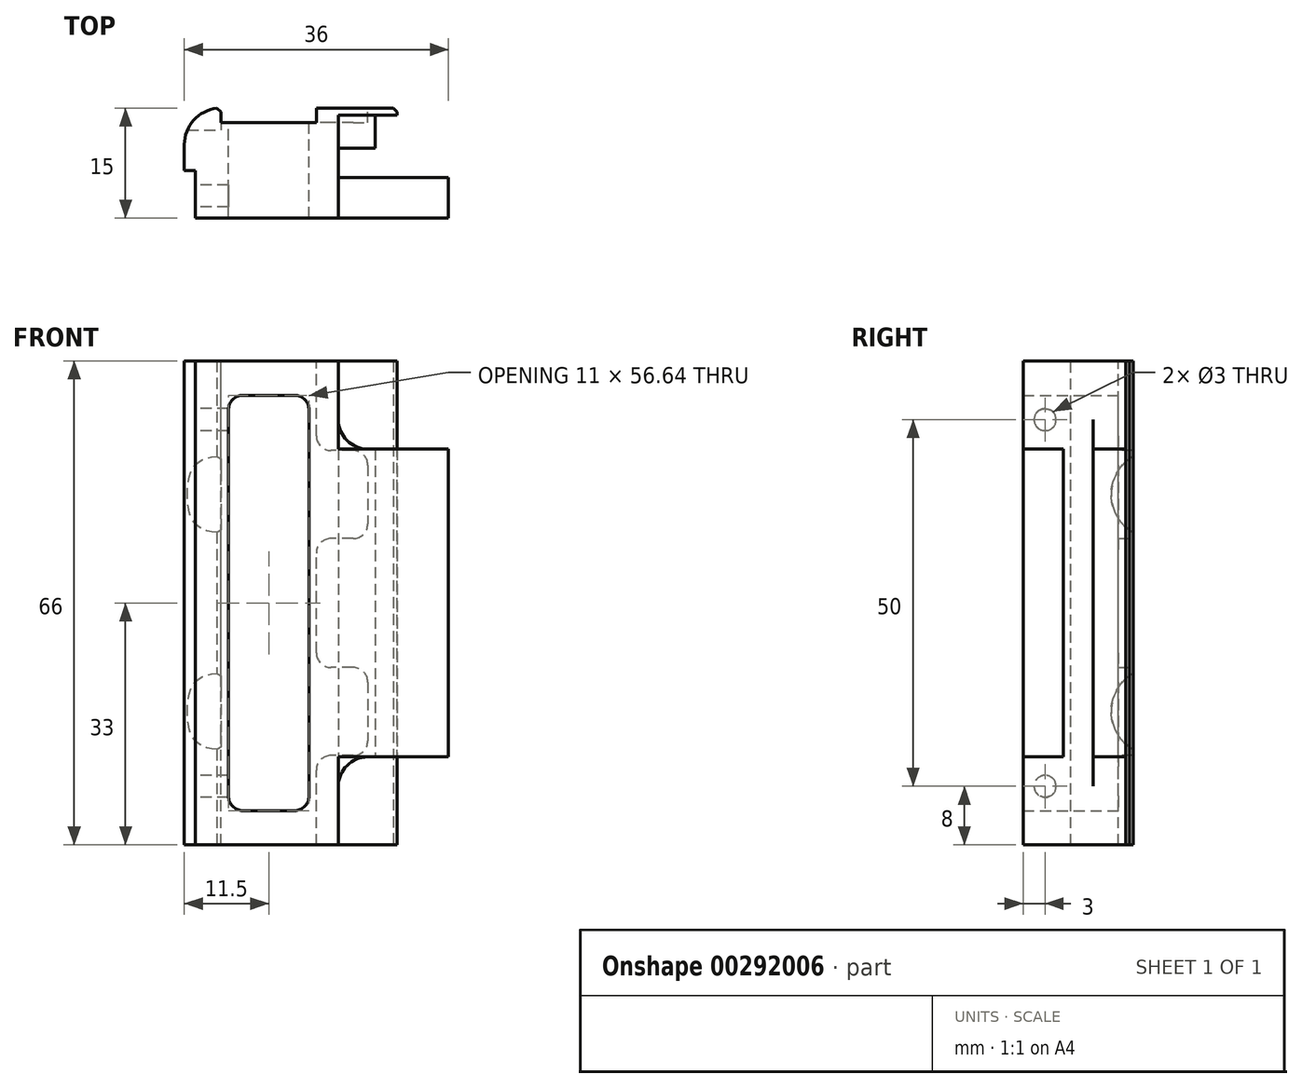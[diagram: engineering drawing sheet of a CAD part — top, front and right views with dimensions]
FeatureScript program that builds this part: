
annotation { "Feature Type Name" : "Feature", "Feature Type Description" : "" }
export const myFeature = defineFeature(function(context is Context, id is Id, definition is map)
    precondition{}
    {
        {
            var Q0;
            Q0=qCreatedBy(makeId("Front.planeOp"),FACE);
            var sketch = newSketch(context, id + "F0", { "sketchPlane" : qUnion([Q0])});
            skLineSegment(sketch, "E0.bottom", {"start": v(5.5, -28.32) * mm, "end": v(-5.5, -28.32) * mm});
            skLineSegment(sketch, "E0.top", {"start": v(5.5, 28.32) * mm, "end": v(-5.5, 28.32) * mm});
            skLineSegment(sketch, "E0.left", {"start": v(5.5, -28.32) * mm, "end": v(5.5, 28.32) * mm});
            skLineSegment(sketch, "E0.right", {"start": v(-5.5, -28.32) * mm, "end": v(-5.5, 28.32) * mm});
            skPoint(sketch, "E0.middle", {"position": v(0, 0) * mm});
            skLineSegment(sketch, "E1.bottom", {"start": v(9.5, -33) * mm, "end": v(-11.5, -33) * mm});
            skLineSegment(sketch, "E1.top", {"start": v(9.5, 33) * mm, "end": v(-11.5, 33) * mm});
            skLineSegment(sketch, "E1.right", {"start": v(-11.5, -33) * mm, "end": v(-11.5, 33) * mm});
            skLineSegment(sketch, "E2", {"start": v(9.5, 33) * mm, "end": v(9.5, -33) * mm});
            skSolve(sketch);
        }
        {
            var Q0;
            Q0=qSketchRegion(id+"F0",true);
            extrude(context, id + "F1", {"entities" : qUnion([Q0]), "depth" : 15 * mm});
        }
        {
            var Q0;
            Q0=makeQuery(id+"F1.opExtrude","CAP_EDGE",EDGE,{"disambiguationData":[OSD([sQuery(id+"F0.wireOp",EDGE,"E1.right")])],"isStart":true});
            fillet(context, id + "F2", {"entities" : qUnion([Q0]), "radius" : 5 * mm, "tangentPropagation" : true, "allowEdgeOverflow" : false});
        }
        {
            var Q0;
            Q0=qCreatedBy(makeId("Front.planeOp"),FACE);
            var sketch = newSketch(context, id + "F3", { "sketchPlane" : qUnion([Q0])});
            skLineSegment(sketch, "E3.bottom", {"start": v(9.5, -21) * mm, "end": v(24.5, -21) * mm});
            skLineSegment(sketch, "E3.top", {"start": v(9.5, 21) * mm, "end": v(24.5, 21) * mm});
            skLineSegment(sketch, "E3.left", {"start": v(9.5, -21) * mm, "end": v(9.5, 21) * mm});
            skLineSegment(sketch, "E3.right", {"start": v(24.5, -21) * mm, "end": v(24.5, 21) * mm});
            skPoint(sketch, "E3.middle", {"position": v(17, 0) * mm});
            skSolve(sketch);
        }
        {
            var Q0;
            Q0=makeQuery(id+"F3.imprint","IMPRINT",FACE,{"disambiguationData":[TD([[makeQuery(id+"F3.imprint","IMPRINT",EDGE,{"derivedFrom":sQuery(id+"F3.wireOp",EDGE,"E3.bottom")}),1.0]])]});
            extrude(context, id + "F4", {"entities" : qUnion([Q0]), "operationType" : NewBodyOperationType.ADD, "depth" : 15 * mm, "hasSecondDirection" : true, "secondDirectionOppositeDirection" : false, "secondDirectionDepth" : 9.5 * mm});
        }
        {
            var Q0;
            Q0=makeQuery(id+"F1.opExtrude","SWEPT_EDGE",EDGE,{"disambiguationData":[OSD([sQuery(id+"F0.wireOp",EDGE,"E0.bottom"),sQuery(id+"F0.wireOp",EDGE,"E0.left")])]});
            var Q1;
            Q1=makeQuery(id+"F1.opExtrude","SWEPT_EDGE",EDGE,{"disambiguationData":[OSD([sQuery(id+"F0.wireOp",EDGE,"E0.bottom"),sQuery(id+"F0.wireOp",EDGE,"E0.right")])]});
            var Q2;
            Q2=makeQuery(id+"F1.opExtrude","SWEPT_EDGE",EDGE,{"disambiguationData":[OSD([sQuery(id+"F0.wireOp",EDGE,"E0.top"),sQuery(id+"F0.wireOp",EDGE,"E0.right")])]});
            var Q3;
            Q3=makeQuery(id+"F1.opExtrude","SWEPT_EDGE",EDGE,{"disambiguationData":[OSD([sQuery(id+"F0.wireOp",EDGE,"E0.top"),sQuery(id+"F0.wireOp",EDGE,"E0.left")])]});
            fillet(context, id + "F5", {"entities" : qUnion([Q0, Q1, Q2, Q3]), "radius" : 2 * mm, "tangentPropagation" : true, "allowEdgeOverflow" : false});
        }
        {
            var Q0;
            Q0=qCreatedBy(makeId("Top.planeOp"),FACE);
            var sketch = newSketch(context, id + "F6", { "sketchPlane" : qUnion([Q0])});
            skLineSegment(sketch, "E4.bottom", {"start": v(-10, -15) * mm, "end": v(-11.5, -15) * mm});
            skLineSegment(sketch, "E4.top", {"start": v(-10, -8.5) * mm, "end": v(-11.5, -8.5) * mm});
            skLineSegment(sketch, "E4.left", {"start": v(-10, -15) * mm, "end": v(-10, -8.5) * mm});
            skLineSegment(sketch, "E4.right", {"start": v(-11.5, -15) * mm, "end": v(-11.5, -8.5) * mm});
            skSolve(sketch);
        }
        {
            var Q0;
            Q0=qSketchRegion(id+"F6",true);
            extrude(context, id + "F7", {"entities" : qUnion([Q0]), "operationType" : NewBodyOperationType.REMOVE, "oppositeDirection" : true, "depth" : 50 * mm, "hasSecondDirection" : true, "secondDirectionOppositeDirection" : false, "secondDirectionDepth" : 50 * mm});
        }
        {
            var Q0;
            Q0=makeQuery(id+"F7.boolean.opBoolean","COPY",FACE,{"derivedFrom":makeQuery(id+"F7.opExtrude","SWEPT_FACE",FACE,{"disambiguationData":[OSD([sQuery(id+"F6.wireOp",EDGE,"E4.left")])]})});
            var sketch = newSketch(context, id + "F8", { "sketchPlane" : qUnion([Q0])});
            skCircle(sketch, "E5", {"center": v(12, 25) * mm, "radius": 1.5 * mm});
            skCircle(sketch, "E6", {"center": v(12, -25) * mm, "radius": 1.5 * mm});
            skSolve(sketch);
        }
        {
            var Q0;
            Q0=qSketchRegion(id+"F8",true);
            extrude(context, id + "F9", {"entities" : qUnion([Q0]), "operationType" : NewBodyOperationType.REMOVE, "oppositeDirection" : true, "depth" : 5 * mm});
        }
        {
            var Q0;
            Q0=qCreatedBy(makeId("Top.planeOp"),FACE);
            var sketch = newSketch(context, id + "F10", { "sketchPlane" : qUnion([Q0])});
            skLineSegment(sketch, "E7.bottom", {"start": v(17.5, -1) * mm, "end": v(14.5, -1) * mm});
            skLineSegment(sketch, "E7.top", {"start": v(17.5, 0) * mm, "end": v(14.5, 0) * mm});
            skLineSegment(sketch, "E7.left", {"start": v(17.5, -1) * mm, "end": v(17.5, 0) * mm});
            skLineSegment(sketch, "E7.right", {"start": v(14.5, -1) * mm, "end": v(14.5, 0) * mm});
            skLineSegment(sketch, "E8.bottom", {"start": v(9.5, 0) * mm, "end": v(14.5, 0) * mm});
            skLineSegment(sketch, "E8.top", {"start": v(9.5, -5.45) * mm, "end": v(14.5, -5.45) * mm});
            skLineSegment(sketch, "E8.left", {"start": v(9.5, 0) * mm, "end": v(9.5, -5.45) * mm});
            skLineSegment(sketch, "E8.right", {"start": v(14.5, 0) * mm, "end": v(14.5, -5.45) * mm});
            skSolve(sketch);
        }
        {
            var Q0;
            Q0=makeQuery(id+"F10.imprint","IMPRINT",FACE,{"disambiguationData":[TD([[makeQuery(id+"F10.imprint","IMPRINT",EDGE,{"derivedFrom":sQuery(id+"F10.wireOp",EDGE,"E7.bottom")}),-1.0]])]});
            var Q1;
            {var subQ2=sQuery(id+"F10.wireOp",EDGE,"E8.bottom");Q1=makeQuery(id+"F10.imprint","IMPRINT",FACE,{"disambiguationData":[TD([[makeQuery(id+"F10.imprint","IMPRINT",EDGE,{"derivedFrom":subQ2}),-1.0]])]});}
            extrude(context, id + "F11", {"entities" : qUnion([Q0, Q1]), "operationType" : NewBodyOperationType.ADD, "depth" : 33 * mm, "hasSecondDirection" : true, "secondDirectionOppositeDirection" : true, "secondDirectionDepth" : 33 * mm});
        }
        {
            var Q0;
            Q0=makeQuery(id+"F11.opExtrude","SWEPT_EDGE",EDGE,{"disambiguationData":[OSD([sQuery(id+"F10.wireOp",EDGE,"E7.top"),sQuery(id+"F10.wireOp",EDGE,"E7.left")])]});
            chamfer(context, id + "F12", {"entities" : qUnion([Q0]), "width" : 0.5 * mm, "tangentPropagation" : true});
        }
        {
            var Q0;
            Q0=makeQuery(id+"F4.boolean.opBoolean","MERGE",FACE,{"derivedFrom":[makeQuery(id+"F1.opExtrude","CAP_FACE",FACE,{"disambiguationData":[OSD([sQuery(id+"F0.wireOp",EDGE,"E0.bottom"),sQuery(id+"F0.wireOp",EDGE,"E0.top"),sQuery(id+"F0.wireOp",EDGE,"E0.left"),sQuery(id+"F0.wireOp",EDGE,"E0.right"),sQuery(id+"F0.wireOp",EDGE,"E1.bottom"),sQuery(id+"F0.wireOp",EDGE,"E1.top"),sQuery(id+"F0.wireOp",EDGE,"E1.right"),sQuery(id+"F0.wireOp",EDGE,"E2")])],"isStart":false}),makeQuery(id+"F4.opExtrude","CAP_FACE",FACE,{"disambiguationData":[OSD([sQuery(id+"F3.wireOp",EDGE,"E3.bottom"),sQuery(id+"F3.wireOp",EDGE,"E3.top"),sQuery(id+"F3.wireOp",EDGE,"E3.left"),sQuery(id+"F3.wireOp",EDGE,"E3.right")])],"isStart":false})]});
            var sketch = newSketch(context, id + "F13", { "sketchPlane" : qUnion([Q0])});
            skLineSegment(sketch, "E9.bottom", {"start": v(9.5, -33) * mm, "end": v(14.5, -33) * mm});
            skLineSegment(sketch, "E9.top", {"start": v(9.5, -21) * mm, "end": v(14.5, -21) * mm});
            skLineSegment(sketch, "E9.left", {"start": v(9.5, -33) * mm, "end": v(9.5, -21) * mm});
            skLineSegment(sketch, "E9.right", {"start": v(14.5, -33) * mm, "end": v(14.5, -21) * mm});
            skLineSegment(sketch, "E10.bottom", {"start": v(9.5, 33) * mm, "end": v(14.5, 33) * mm});
            skLineSegment(sketch, "E10.top", {"start": v(9.5, 21) * mm, "end": v(14.5, 21) * mm});
            skLineSegment(sketch, "E10.left", {"start": v(9.5, 33) * mm, "end": v(9.5, 21) * mm});
            skLineSegment(sketch, "E10.right", {"start": v(14.5, 33) * mm, "end": v(14.5, 21) * mm});
            skSolve(sketch);
        }
        {
            var Q0;
            Q0=qSketchRegion(id+"F13",true);
            extrude(context, id + "F14", {"entities" : qUnion([Q0]), "operationType" : NewBodyOperationType.REMOVE, "oppositeDirection" : true, "depth" : 14 * mm});
        }
        {
            var Q0;
            Q0=makeQuery(id+"F14.boolean.opBoolean","COPY",EDGE,{"derivedFrom":makeQuery(id+"F14.opExtrude","SWEPT_EDGE",EDGE,{"disambiguationData":[OSD([sQuery(id+"F13.wireOp",EDGE,"E9.top"),sQuery(id+"F13.wireOp",EDGE,"E9.left")])]})});
            var Q1;
            Q1=makeQuery(id+"F14.boolean.opBoolean","COPY",EDGE,{"derivedFrom":makeQuery(id+"F14.opExtrude","SWEPT_EDGE",EDGE,{"disambiguationData":[OSD([sQuery(id+"F13.wireOp",EDGE,"E10.top"),sQuery(id+"F13.wireOp",EDGE,"E10.left")])]})});
            var Q2;
            Q2=makeQuery(id+"F4.opExtrude","SWEPT_EDGE",EDGE,{"disambiguationData":[OSD([sQuery(id+"F3.wireOp",EDGE,"E3.top"),sQuery(id+"F3.wireOp",EDGE,"E3.left")])]});
            var Q3;
            Q3=makeQuery(id+"F4.opExtrude","SWEPT_EDGE",EDGE,{"disambiguationData":[OSD([sQuery(id+"F3.wireOp",EDGE,"E3.bottom"),sQuery(id+"F3.wireOp",EDGE,"E3.left")])]});
            fillet(context, id + "F15", {"entities" : qUnion([Q0, Q1, Q2, Q3]), "radius" : 4 * mm, "tangentPropagation" : true, "allowEdgeOverflow" : false});
        }
        {
            var Q0;
            Q0=qCreatedBy(makeId("Front.planeOp"),FACE);
            var sketch = newSketch(context, id + "F16", { "sketchPlane" : qUnion([Q0])});
            skLineSegment(sketch, "E11.bottom", {"start": v(-6.5, -35) * mm, "end": v(6.5, -35) * mm});
            skLineSegment(sketch, "E11.top", {"start": v(-6.5, 35) * mm, "end": v(6.5, 35) * mm});
            skLineSegment(sketch, "E11.left", {"start": v(-6.5, -35) * mm, "end": v(-6.5, 35) * mm});
            skLineSegment(sketch, "E11.right", {"start": v(6.5, -35) * mm, "end": v(6.5, 35) * mm});
            skPoint(sketch, "E11.middle", {"position": v(0, 0) * mm});
            skSolve(sketch);
        }
        {
            var Q0;
            Q0=makeQuery(id+"F16.imprint","IMPRINT",FACE,{"disambiguationData":[TD([[makeQuery(id+"F16.imprint","IMPRINT",EDGE,{"derivedFrom":sQuery(id+"F16.wireOp",EDGE,"E11.bottom")}),1.0]])]});
            extrude(context, id + "F17", {"entities" : qUnion([Q0]), "operationType" : NewBodyOperationType.REMOVE, "depth" : 2 * mm});
        }
        {
            var Q0;
            Q0=makeQuery(id+"F11.boolean.opBoolean","MERGE",FACE,{"derivedFrom":[makeQuery(id+"F1.opExtrude","CAP_FACE",FACE,{"disambiguationData":[OSD([sQuery(id+"F0.wireOp",EDGE,"E0.bottom"),sQuery(id+"F0.wireOp",EDGE,"E0.top"),sQuery(id+"F0.wireOp",EDGE,"E0.left"),sQuery(id+"F0.wireOp",EDGE,"E0.right"),sQuery(id+"F0.wireOp",EDGE,"E1.bottom"),sQuery(id+"F0.wireOp",EDGE,"E1.top"),sQuery(id+"F0.wireOp",EDGE,"E1.right"),sQuery(id+"F0.wireOp",EDGE,"E2")])],"isStart":true}),makeQuery(id+"F11.opExtrude","SWEPT_FACE",FACE,{"disambiguationData":[OSD([sQuery(id+"F10.wireOp",EDGE,"E7.top"),sQuery(id+"F10.wireOp",EDGE,"E8.bottom")])]})]});
            var sketch = newSketch(context, id + "F18", { "sketchPlane" : qUnion([Q0])});
            skLineSegment(sketch, "E12.bottom", {"start": v(-13.5, 20.8) * mm, "end": v(6.5, 20.8) * mm});
            skLineSegment(sketch, "E12.top", {"start": v(-13.5, 8.8) * mm, "end": v(6.5, 8.8) * mm});
            skLineSegment(sketch, "E12.left", {"start": v(-13.5, 20.8) * mm, "end": v(-13.5, 8.8) * mm});
            skLineSegment(sketch, "E12.right", {"start": v(6.5, 20.8) * mm, "end": v(6.5, 8.8) * mm});
            skPoint(sketch, "E12.middle", {"position": v(-3.5, 14.8) * mm});
            skLineSegment(sketch, "E13.bottom", {"start": v(-13.5, -8.8) * mm, "end": v(6.5, -8.8) * mm});
            skLineSegment(sketch, "E13.top", {"start": v(-13.5, -20.8) * mm, "end": v(6.5, -20.8) * mm});
            skLineSegment(sketch, "E13.left", {"start": v(-13.5, -8.8) * mm, "end": v(-13.5, -20.8) * mm});
            skLineSegment(sketch, "E13.right", {"start": v(6.5, -8.8) * mm, "end": v(6.5, -20.8) * mm});
            skPoint(sketch, "E13.middle", {"position": v(-3.5, -14.8) * mm});
            skSolve(sketch);
        }
        {
            var Q0;
            Q0=qSketchRegion(id+"F18",true);
            extrude(context, id + "F19", {"entities" : qUnion([Q0]), "operationType" : NewBodyOperationType.REMOVE, "oppositeDirection" : true, "depth" : 2 * mm});
        }
        {
            var Q0;
            Q0=makeQuery(id+"F19.boolean.opBoolean","COPY",EDGE,{"derivedFrom":makeQuery(id+"F19.opExtrude","SWEPT_EDGE",EDGE,{"disambiguationData":[OSD([sQuery(id+"F18.wireOp",EDGE,"E13.top"),sQuery(id+"F18.wireOp",EDGE,"E13.left")])]})});
            var Q1;
            Q1=makeQuery(id+"F19.boolean.opBoolean","COPY",EDGE,{"derivedFrom":makeQuery(id+"F19.opExtrude","SWEPT_EDGE",EDGE,{"disambiguationData":[OSD([sQuery(id+"F18.wireOp",EDGE,"E12.bottom"),sQuery(id+"F18.wireOp",EDGE,"E12.left")])]})});
            var Q2;
            Q2=makeQuery(id+"F19.boolean.opBoolean","INTERSECT",EDGE,{"derivedFrom":[makeQuery(id+"F17.boolean.opBoolean","COPY",FACE,{"derivedFrom":makeQuery(id+"F17.opExtrude","SWEPT_FACE",FACE,{"disambiguationData":[OSD([sQuery(id+"F16.wireOp",EDGE,"E11.right")])]})}),makeQuery(id+"F19.opExtrude","SWEPT_FACE",FACE,{"disambiguationData":[OSD([sQuery(id+"F18.wireOp",EDGE,"E12.bottom")])]})]});
            var Q3;
            Q3=makeQuery(id+"F19.boolean.opBoolean","INTERSECT",EDGE,{"derivedFrom":[makeQuery(id+"F17.boolean.opBoolean","COPY",FACE,{"derivedFrom":makeQuery(id+"F17.opExtrude","SWEPT_FACE",FACE,{"disambiguationData":[OSD([sQuery(id+"F16.wireOp",EDGE,"E11.right")])]})}),makeQuery(id+"F19.opExtrude","SWEPT_FACE",FACE,{"disambiguationData":[OSD([sQuery(id+"F18.wireOp",EDGE,"E12.top")])]})]});
            var Q4;
            Q4=makeQuery(id+"F19.boolean.opBoolean","INTERSECT",EDGE,{"derivedFrom":[makeQuery(id+"F17.boolean.opBoolean","COPY",FACE,{"derivedFrom":makeQuery(id+"F17.opExtrude","SWEPT_FACE",FACE,{"disambiguationData":[OSD([sQuery(id+"F16.wireOp",EDGE,"E11.right")])]})}),makeQuery(id+"F19.opExtrude","SWEPT_FACE",FACE,{"disambiguationData":[OSD([sQuery(id+"F18.wireOp",EDGE,"E13.bottom")])]})]});
            var Q5;
            Q5=makeQuery(id+"F19.boolean.opBoolean","INTERSECT",EDGE,{"derivedFrom":[makeQuery(id+"F17.boolean.opBoolean","COPY",FACE,{"derivedFrom":makeQuery(id+"F17.opExtrude","SWEPT_FACE",FACE,{"disambiguationData":[OSD([sQuery(id+"F16.wireOp",EDGE,"E11.right")])]})}),makeQuery(id+"F19.opExtrude","SWEPT_FACE",FACE,{"disambiguationData":[OSD([sQuery(id+"F18.wireOp",EDGE,"E13.top")])]})]});
            var Q6;
            Q6=makeQuery(id+"F19.boolean.opBoolean","COPY",EDGE,{"derivedFrom":makeQuery(id+"F19.opExtrude","SWEPT_EDGE",EDGE,{"disambiguationData":[OSD([sQuery(id+"F18.wireOp",EDGE,"E13.bottom"),sQuery(id+"F18.wireOp",EDGE,"E13.left")])]})});
            var Q7;
            Q7=makeQuery(id+"F19.boolean.opBoolean","COPY",EDGE,{"derivedFrom":makeQuery(id+"F19.opExtrude","SWEPT_EDGE",EDGE,{"disambiguationData":[OSD([sQuery(id+"F18.wireOp",EDGE,"E12.top"),sQuery(id+"F18.wireOp",EDGE,"E12.left")])]})});
            fillet(context, id + "F20", {"entities" : qUnion([Q0, Q1, Q2, Q3, Q4, Q5, Q6, Q7]), "radius" : 2 * mm, "tangentPropagation" : true, "allowEdgeOverflow" : false});
        }
        {
            var Q0;
            {var subQ0=sQuery(id+"F0.wireOp",EDGE,"E1.right");Q0=makeQuery(id+"F17.boolean.opBoolean","MERGE",EDGE,{"derivedFrom":[makeQuery(id+"F2.opFillet","BLEND_EDGE",EDGE,{"blendedFrom":[makeQuery(id+"F1.opExtrude","CAP_EDGE",EDGE,{"disambiguationData":[OSD([subQ0])],"isStart":true}),makeQuery(id+"F1.opExtrude","CAP_FACE",FACE,{"disambiguationData":[OSD([sQuery(id+"F0.wireOp",EDGE,"E0.bottom"),sQuery(id+"F0.wireOp",EDGE,"E0.top"),sQuery(id+"F0.wireOp",EDGE,"E0.left"),sQuery(id+"F0.wireOp",EDGE,"E0.right"),sQuery(id+"F0.wireOp",EDGE,"E1.bottom"),sQuery(id+"F0.wireOp",EDGE,"E1.top"),subQ0,sQuery(id+"F0.wireOp",EDGE,"E2")])],"isStart":true})],"blendedInto":[makeQuery(id+"F1.opExtrude","CAP_FACE",FACE,{"disambiguationData":[OSD([sQuery(id+"F0.wireOp",EDGE,"E0.bottom"),sQuery(id+"F0.wireOp",EDGE,"E0.top"),sQuery(id+"F0.wireOp",EDGE,"E0.left"),sQuery(id+"F0.wireOp",EDGE,"E0.right"),sQuery(id+"F0.wireOp",EDGE,"E1.bottom"),sQuery(id+"F0.wireOp",EDGE,"E1.top"),subQ0,sQuery(id+"F0.wireOp",EDGE,"E2")])],"isStart":true})]}),makeQuery(id+"F17.opExtrude","CAP_EDGE",EDGE,{"disambiguationData":[OSD([sQuery(id+"F16.wireOp",EDGE,"E11.left")])],"isStart":true})]});}
            var Q1;
            {var subQ2=sQuery(id+"F0.wireOp",EDGE,"E1.bottom");var subQ3=sQuery(id+"F16.wireOp",EDGE,"E11.right");Q1=makeQuery(id+"F19.boolean.opBoolean","SPLIT",EDGE,{"disambiguationData":[TD([makeQuery(id+"F1.opExtrude","SWEPT_FACE",FACE,{"disambiguationData":[OSD([subQ2])]})])],"derivedFrom":makeQuery(id+"F17.boolean.opBoolean","COPY",EDGE,{"derivedFrom":makeQuery(id+"F17.opExtrude","CAP_EDGE",EDGE,{"disambiguationData":[OSD([subQ3])],"isStart":true})})});}
            chamfer(context, id + "F21", {"entities" : qUnion([Q0, Q1]), "width" : 0.5 * mm, "tangentPropagation" : true});
        }
        {
            var Q0;
            Q0=qCreatedBy(makeId("Right.planeOp"),FACE);
            var sketch = newSketch(context, id + "F22", { "sketchPlane" : qUnion([Q0])});
            skCircle(sketch, "E14", {"center": v(3, -14.8) * mm, "radius": 6 * mm});
            skCircle(sketch, "E15", {"center": v(3, 14.8) * mm, "radius": 6 * mm});
            skLineSegment(sketch, "E16", {"start": v(3, -14.8) * mm, "end": v(3, 14.8) * mm, "construction": true});
            skSolve(sketch);
        }
        {
            var Q0;
            Q0=qSketchRegion(id+"F22",true);
            extrude(context, id + "F23", {"entities" : qUnion([Q0]), "operationType" : NewBodyOperationType.REMOVE, "endBound" : BoundingType.THROUGH_ALL, "oppositeDirection" : true, "depth" : 25 * mm, "hasSecondDirection" : true, "secondDirectionOppositeDirection" : true, "secondDirectionDepth" : 6.5 * mm});
        }
    });
